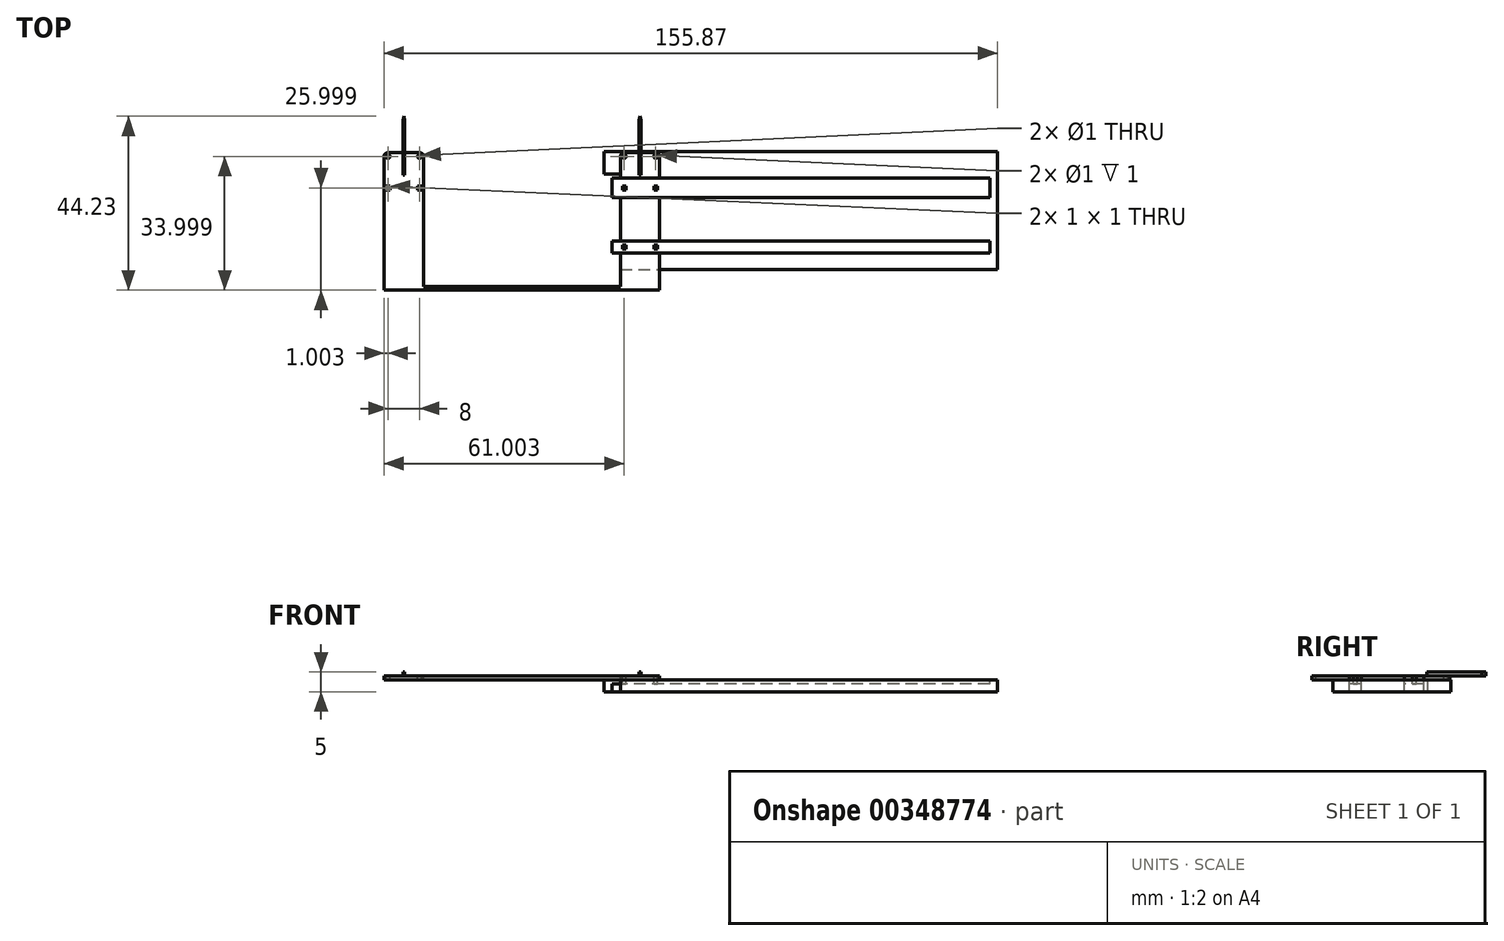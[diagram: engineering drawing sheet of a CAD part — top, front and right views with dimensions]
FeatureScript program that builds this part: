
annotation { "Feature Type Name" : "Feature", "Feature Type Description" : "" }
export const myFeature = defineFeature(function(context is Context, id is Id, definition is map)
    precondition{}
    {
        {
            var Q0;
            Q0=qCreatedBy(makeId("Top.planeOp"),FACE);
            var sketch = newSketch(context, id + "F0", { "sketchPlane" : qUnion([Q0])});
            skLineSegment(sketch, "E0.bottom", {"start": v(4.13, -30.56) * mm, "end": v(14.13, -30.56) * mm});
            skLineSegment(sketch, "E0.top", {"start": v(5.13, -20.56) * mm, "end": v(13.13, -20.56) * mm});
            skLineSegment(sketch, "E0.left", {"start": v(4.13, -30.56) * mm, "end": v(4.13, -21.56) * mm});
            skLineSegment(sketch, "E0.right", {"start": v(14.13, -30.56) * mm, "end": v(14.13, -21.56) * mm});
            skCircle(sketch, "E1", {"center": v(5.13, -21.56) * mm, "radius": 0.5 * mm});
            skLineSegment(sketch, "E2", {"start": v(14.13, -20.56) * mm, "end": v(16.75, -17.94) * mm, "construction": true});
            skCircle(sketch, "E3.MirrorC", {"center": v(13.13, -29.56) * mm, "radius": 0.5 * mm, "construction": true});
            skCircle(sketch, "E4", {"center": v(5.13, -29.56) * mm, "radius": 0.5 * mm, "construction": true});
            skCircle(sketch, "E5", {"center": v(13.13, -21.56) * mm, "radius": 0.5 * mm});
            skPoint(sketch, "E6.visualSharp", {"position": v(4.13, -20.56) * mm});
            skArc(sketch, "E6.filletArc", {"start": v(5.13, -20.56) * mm, "mid": v(4.43, -20.85) * mm, "end": v(4.13, -21.56) * mm});
            skPoint(sketch, "E7.visualSharp", {"position": v(14.13, -20.56) * mm});
            skArc(sketch, "E7.filletArc", {"start": v(14.13, -21.56) * mm, "mid": v(13.84, -20.85) * mm, "end": v(13.13, -20.56) * mm});
            skCircle(sketch, "E8", {"center": v(5.13, -44.56) * mm, "radius": 0.5 * mm, "construction": true});
            skCircle(sketch, "E9", {"center": v(13.13, -44.56) * mm, "radius": 0.5 * mm, "construction": true});
            skLineSegment(sketch, "E10.bottom", {"start": v(5.63, -29.06) * mm, "end": v(4.63, -29.06) * mm});
            skLineSegment(sketch, "E10.top", {"start": v(5.63, -30.06) * mm, "end": v(4.63, -30.06) * mm});
            skLineSegment(sketch, "E10.left", {"start": v(5.63, -29.06) * mm, "end": v(5.63, -30.06) * mm});
            skLineSegment(sketch, "E10.right", {"start": v(4.63, -29.06) * mm, "end": v(4.63, -30.06) * mm});
            skLineSegment(sketch, "E11.bottom", {"start": v(13.63, -29.06) * mm, "end": v(12.63, -29.06) * mm});
            skLineSegment(sketch, "E11.top", {"start": v(13.63, -30.06) * mm, "end": v(12.63, -30.06) * mm});
            skLineSegment(sketch, "E11.left", {"start": v(13.63, -29.06) * mm, "end": v(13.63, -30.06) * mm});
            skLineSegment(sketch, "E11.right", {"start": v(12.63, -29.06) * mm, "end": v(12.63, -30.06) * mm});
            skLineSegment(sketch, "E12.bottom", {"start": v(5.63, -44.06) * mm, "end": v(4.63, -44.06) * mm});
            skLineSegment(sketch, "E12.top", {"start": v(5.63, -45.06) * mm, "end": v(4.63, -45.06) * mm});
            skLineSegment(sketch, "E12.left", {"start": v(5.63, -44.06) * mm, "end": v(5.63, -45.06) * mm});
            skLineSegment(sketch, "E12.right", {"start": v(4.63, -44.06) * mm, "end": v(4.63, -45.06) * mm});
            skLineSegment(sketch, "E13.bottom", {"start": v(13.63, -44.06) * mm, "end": v(12.63, -44.06) * mm});
            skLineSegment(sketch, "E13.top", {"start": v(13.63, -45.06) * mm, "end": v(12.63, -45.06) * mm});
            skLineSegment(sketch, "E13.left", {"start": v(13.63, -44.06) * mm, "end": v(13.63, -45.06) * mm});
            skLineSegment(sketch, "E13.right", {"start": v(12.63, -44.06) * mm, "end": v(12.63, -45.06) * mm});
            skLineSegment(sketch, "E14", {"start": v(-20.87, -13.48) * mm, "end": v(-20.87, -4.13) * mm, "construction": true});
            skLineSegment(sketch, "E15.MirrorCS", {"start": v(-47.37, -45.06) * mm, "end": v(-46.37, -45.06) * mm});
            skLineSegment(sketch, "E16.MirrorCS", {"start": v(-47.37, -44.06) * mm, "end": v(-46.37, -44.06) * mm});
            skLineSegment(sketch, "E17.MirrorCS", {"start": v(-46.37, -29.06) * mm, "end": v(-46.37, -30.06) * mm});
            skLineSegment(sketch, "E18.MirrorCS", {"start": v(-47.37, -30.06) * mm, "end": v(-46.37, -30.06) * mm});
            skLineSegment(sketch, "E19.MirrorCS", {"start": v(-55.37, -30.06) * mm, "end": v(-54.37, -30.06) * mm});
            skLineSegment(sketch, "E20.MirrorCS", {"start": v(-46.37, -44.06) * mm, "end": v(-46.37, -45.06) * mm});
            skLineSegment(sketch, "E21.MirrorCS", {"start": v(-47.37, -29.06) * mm, "end": v(-46.37, -29.06) * mm});
            skLineSegment(sketch, "E22.MirrorCS", {"start": v(-47.37, -44.06) * mm, "end": v(-47.37, -45.06) * mm});
            skCircle(sketch, "E23.MirrorC", {"center": v(-46.87, -29.56) * mm, "radius": 0.5 * mm, "construction": true});
            skLineSegment(sketch, "E24.MirrorCS", {"start": v(-55.37, -29.06) * mm, "end": v(-54.37, -29.06) * mm});
            skCircle(sketch, "E25.MirrorC", {"center": v(-46.87, -44.56) * mm, "radius": 0.5 * mm, "construction": true});
            skLineSegment(sketch, "E26.MirrorCS", {"start": v(-47.37, -29.06) * mm, "end": v(-47.37, -30.06) * mm});
            skLineSegment(sketch, "E27.MirrorCS", {"start": v(-54.37, -44.06) * mm, "end": v(-54.37, -45.06) * mm});
            skLineSegment(sketch, "E28.MirrorCS", {"start": v(-55.37, -44.06) * mm, "end": v(-54.37, -44.06) * mm});
            skCircle(sketch, "E29.MirrorC", {"center": v(-54.87, -29.56) * mm, "radius": 0.5 * mm, "construction": true});
            skLineSegment(sketch, "E30.MirrorCS", {"start": v(-54.37, -29.06) * mm, "end": v(-54.37, -30.06) * mm});
            skLineSegment(sketch, "E31.MirrorCS", {"start": v(-55.37, -29.06) * mm, "end": v(-55.37, -30.06) * mm});
            skLineSegment(sketch, "E32.MirrorCS", {"start": v(-55.37, -44.06) * mm, "end": v(-55.37, -45.06) * mm});
            skCircle(sketch, "E33.MirrorC", {"center": v(-54.87, -44.56) * mm, "radius": 0.5 * mm, "construction": true});
            skCircle(sketch, "E34.MirrorC", {"center": v(-54.87, -21.56) * mm, "radius": 0.5 * mm});
            skLineSegment(sketch, "E35.MirrorCS", {"start": v(-55.37, -45.06) * mm, "end": v(-54.37, -45.06) * mm});
            skArc(sketch, "E36.MirrorCS", {"start": v(-46.87, -20.56) * mm, "mid": v(-46.16, -20.85) * mm, "end": v(-45.87, -21.56) * mm});
            skArc(sketch, "E37.MirrorCS", {"start": v(-55.87, -21.56) * mm, "mid": v(-55.57, -20.85) * mm, "end": v(-54.87, -20.56) * mm});
            skCircle(sketch, "E38.MirrorC", {"center": v(-46.87, -21.56) * mm, "radius": 0.5 * mm});
            skLineSegment(sketch, "E39.MirrorCS", {"start": v(-55.87, -20.56) * mm, "end": v(-58.48, -17.94) * mm, "construction": true});
            skLineSegment(sketch, "E40.MirrorCS", {"start": v(-46.87, -20.56) * mm, "end": v(-54.87, -20.56) * mm});
            skLineSegment(sketch, "E41.MirrorCS", {"start": v(-45.87, -30.56) * mm, "end": v(-55.87, -30.56) * mm});
            skLineSegment(sketch, "E42.MirrorCS", {"start": v(-45.87, -30.56) * mm, "end": v(-45.87, -21.56) * mm});
            skLineSegment(sketch, "E43.MirrorCS", {"start": v(-55.87, -30.56) * mm, "end": v(-55.87, -21.56) * mm});
            skPoint(sketch, "E44.MirrorP", {"position": v(-55.87, -20.56) * mm});
            skPoint(sketch, "E45.MirrorP", {"position": v(-45.87, -20.56) * mm});
            skLineSegment(sketch, "E46.bottom", {"start": v(-45.87, -30.56) * mm, "end": v(4.13, -30.56) * mm});
            skLineSegment(sketch, "E46.top", {"start": v(-45.87, -26.06) * mm, "end": v(4.13, -26.06) * mm});
            skLineSegment(sketch, "E46.left", {"start": v(-45.87, -30.56) * mm, "end": v(-45.87, -26.06) * mm});
            skLineSegment(sketch, "E46.right", {"start": v(4.13, -30.56) * mm, "end": v(4.13, -26.06) * mm});
            skSolve(sketch);
        }
        {
            var Q0;
            Q0=makeQuery(id+"F0.imprint","IMPRINT",FACE,{"disambiguationData":[TD([[makeQuery(id+"F0.imprint","IMPRINT",EDGE,{"derivedFrom":sQuery(id+"F0.wireOp",EDGE,"E0.bottom")}),1.0]])]});
            var Q1;
            Q1=makeQuery(id+"F0.imprint","IMPRINT",FACE,{"disambiguationData":[TD([[makeQuery(id+"F0.imprint","IMPRINT",EDGE,{"derivedFrom":sQuery(id+"F0.wireOp",EDGE,"E17.MirrorCS")}),1.0]])]});
            var Q2;
            Q2=makeQuery(id+"F0.imprint","IMPRINT",FACE,{"disambiguationData":[TD([[makeQuery(id+"F0.imprint","IMPRINT",EDGE,{"derivedFrom":sQuery(id+"F0.wireOp",EDGE,"E46.bottom")}),1.0]])]});
            extrude(context, id + "F1", {"entities" : qUnion([Q0, Q1, Q2]), "oppositeDirection" : true, "depth" : 1 * mm});
        }
        {
            var Q0;
            Q0=makeQuery(id+"F1.opExtrude","CAP_FACE",FACE,{"disambiguationData":[OSD([sQuery(id+"F0.wireOp",EDGE,"E0.bottom"),sQuery(id+"F0.wireOp",EDGE,"E0.top"),sQuery(id+"F0.wireOp",EDGE,"E0.left"),sQuery(id+"F0.wireOp",EDGE,"E0.right"),sQuery(id+"F0.wireOp",EDGE,"E1"),sQuery(id+"F0.wireOp",EDGE,"E3.MirrorC"),sQuery(id+"F0.wireOp",EDGE,"E4"),sQuery(id+"F0.wireOp",EDGE,"E5"),sQuery(id+"F0.wireOp",EDGE,"E6.filletArc"),sQuery(id+"F0.wireOp",EDGE,"E7.filletArc")])],"isStart":true});
            var sketch = newSketch(context, id + "F2", { "sketchPlane" : qUnion([Q0])});
            skLineSegment(sketch, "E47", {"start": v(9.13, -11.33) * mm, "end": v(9.13, -5.3) * mm, "construction": true});
            skPoint(sketch, "E47.startSnap0", {"position": v(9.13, -20.56) * mm});
            skLineSegment(sketch, "E48", {"start": v(9.13, -11.33) * mm, "end": v(8.9, -12.33) * mm});
            skLineSegment(sketch, "E49.MirrorCS", {"start": v(9.13, -11.33) * mm, "end": v(9.37, -12.33) * mm});
            skLineSegment(sketch, "E50", {"start": v(8.9, -12.33) * mm, "end": v(9.37, -12.33) * mm});
            skLineSegment(sketch, "E51.top", {"start": v(8.9, -26.33) * mm, "end": v(9.37, -26.33) * mm});
            skLineSegment(sketch, "E51.left", {"start": v(8.9, -12.33) * mm, "end": v(8.9, -26.33) * mm});
            skLineSegment(sketch, "E51.right", {"start": v(9.37, -12.33) * mm, "end": v(9.37, -26.33) * mm});
            skLineSegment(sketch, "E52.MirrorCS", {"start": v(-50.63, -12.33) * mm, "end": v(-50.63, -26.33) * mm});
            skLineSegment(sketch, "E53.MirrorCS", {"start": v(-51.1, -12.33) * mm, "end": v(-51.1, -26.33) * mm});
            skLineSegment(sketch, "E54.MirrorCS", {"start": v(-50.87, -11.33) * mm, "end": v(-51.1, -12.33) * mm});
            skLineSegment(sketch, "E55.MirrorCS", {"start": v(-50.87, -11.33) * mm, "end": v(-50.63, -12.33) * mm});
            skLineSegment(sketch, "E56.MirrorCS", {"start": v(-50.63, -12.33) * mm, "end": v(-51.1, -12.33) * mm});
            skLineSegment(sketch, "E57.MirrorCS", {"start": v(-50.87, -11.33) * mm, "end": v(-50.87, -5.3) * mm, "construction": true});
            skLineSegment(sketch, "E58.MirrorCS", {"start": v(-50.63, -26.33) * mm, "end": v(-51.1, -26.33) * mm});
            skSolve(sketch);
        }
        {
            var Q0;
            Q0 = qSketchRegion(id + "F2", true);
            extrude(context, id + "F3", {"entities" : qUnion([Q0]), "depth" : 1 * mm});
        }
        {
            var Q0;
            Q0=qCreatedBy(makeId("Top.planeOp"),FACE);
            var sketch = newSketch(context, id + "F4", { "sketchPlane" : qUnion([Q0])});
            skLineSegment(sketch, "E59.bottom", {"start": v(0, -20.29) * mm, "end": v(100, -20.29) * mm});
            skLineSegment(sketch, "E59.top", {"start": v(0, -50.29) * mm, "end": v(100, -50.29) * mm});
            skLineSegment(sketch, "E59.left", {"start": v(0, -20.29) * mm, "end": v(0, -50.29) * mm});
            skLineSegment(sketch, "E59.right", {"start": v(100, -20.29) * mm, "end": v(100, -50.29) * mm});
            skLineSegment(sketch, "E60.bottom", {"start": v(98, -27.06) * mm, "end": v(2, -27.06) * mm});
            skLineSegment(sketch, "E60.top", {"start": v(98, -32.06) * mm, "end": v(2, -32.06) * mm});
            skLineSegment(sketch, "E60.left", {"start": v(98, -27.06) * mm, "end": v(98, -32.06) * mm});
            skLineSegment(sketch, "E60.right", {"start": v(2, -27.06) * mm, "end": v(2, -32.06) * mm});
            skPoint(sketch, "E60.middle", {"position": v(50, -29.56) * mm});
            skPoint(sketch, "E60.middle.positionSnap0", {"position": v(50, -20.29) * mm});
            skPoint(sketch, "E60.centerSnap0", {"position": v(50, -20.29) * mm});
            skLineSegment(sketch, "E61.bottom", {"start": v(2, -43.06) * mm, "end": v(98, -43.06) * mm});
            skLineSegment(sketch, "E61.top", {"start": v(2, -46.06) * mm, "end": v(98, -46.06) * mm});
            skLineSegment(sketch, "E61.left", {"start": v(2, -43.06) * mm, "end": v(2, -46.06) * mm});
            skLineSegment(sketch, "E61.right", {"start": v(98, -43.06) * mm, "end": v(98, -46.06) * mm});
            skPoint(sketch, "E61.middle", {"position": v(50, -44.56) * mm});
            skPoint(sketch, "E62", {"position": v(2, -44.56) * mm});
            skPoint(sketch, "E63", {"position": v(2, -29.56) * mm});
            skSolve(sketch);
        }
        {
            var Q0;
            Q0=makeQuery(id+"F4.imprint","IMPRINT",FACE,{"disambiguationData":[TD([[makeQuery(id+"F4.imprint","IMPRINT",EDGE,{"derivedFrom":sQuery(id+"F4.wireOp",EDGE,"E59.bottom")}),-1.0]])]});
            var Q1;
            Q1=makeQuery(id+"F4.imprint","IMPRINT",FACE,{"disambiguationData":[TD([[makeQuery(id+"F4.imprint","IMPRINT",EDGE,{"derivedFrom":sQuery(id+"F4.wireOp",EDGE,"E61.bottom")}),-1.0]])]});
            var Q2;
            Q2=makeQuery(id+"F4.imprint","IMPRINT",FACE,{"disambiguationData":[TD([[makeQuery(id+"F4.imprint","IMPRINT",EDGE,{"derivedFrom":sQuery(id+"F4.wireOp",EDGE,"E60.bottom")}),1.0]])]});
            extrude(context, id + "F5", {"entities" : qUnion([Q0, Q1, Q2]), "oppositeDirection" : true, "depth" : 4 * mm, "hasSecondDirection" : true, "secondDirectionOppositeDirection" : true, "secondDirectionDepth" : 1 * mm});
        }
        {
            var Q0;
            Q0=makeQuery(id+"F1.opExtrude","SWEPT_FACE",FACE,{"disambiguationData":[OSD([sQuery(id+"F0.wireOp",EDGE,"E0.bottom")])]});
            extrude(context, id + "F6", {"entities" : qUnion([Q0]), "operationType" : NewBodyOperationType.ADD, "depth" : 25 * mm});
        }
        {
            var Q0;
            Q0=makeQuery(id+"F4.imprint","IMPRINT",FACE,{"disambiguationData":[TD([[makeQuery(id+"F4.imprint","IMPRINT",EDGE,{"derivedFrom":sQuery(id+"F4.wireOp",EDGE,"E60.bottom")}),1.0]])]});
            var Q1;
            Q1=makeQuery(id+"F4.imprint","IMPRINT",FACE,{"disambiguationData":[TD([[makeQuery(id+"F4.imprint","IMPRINT",EDGE,{"derivedFrom":sQuery(id+"F4.wireOp",EDGE,"E61.bottom")}),-1.0]])]});
            extrude(context, id + "F7", {"entities" : qUnion([Q0, Q1]), "operationType" : NewBodyOperationType.REMOVE, "oppositeDirection" : true, "depth" : 2 * mm});
        }
        {
            var Q0;
            Q0=makeQuery(id+"F0.imprint","IMPRINT",FACE,{"disambiguationData":[TD([[makeQuery(id+"F0.imprint","IMPRINT",EDGE,{"derivedFrom":sQuery(id+"F0.wireOp",EDGE,"E13.bottom")}),1.0]])]});
            var Q1;
            Q1=makeQuery(id+"F0.imprint","IMPRINT",FACE,{"disambiguationData":[TD([[makeQuery(id+"F0.imprint","IMPRINT",EDGE,{"derivedFrom":sQuery(id+"F0.wireOp",EDGE,"E12.bottom")}),1.0]])]});
            var Q2;
            Q2=makeQuery(id+"F0.imprint","IMPRINT",FACE,{"disambiguationData":[TD([[makeQuery(id+"F0.imprint","IMPRINT",EDGE,{"derivedFrom":sQuery(id+"F0.wireOp",EDGE,"E10.bottom")}),1.0]])]});
            var Q3;
            Q3=makeQuery(id+"F0.imprint","IMPRINT",FACE,{"disambiguationData":[TD([[makeQuery(id+"F0.imprint","IMPRINT",EDGE,{"derivedFrom":sQuery(id+"F0.wireOp",EDGE,"E11.bottom")}),1.0]])]});
            var Q4;
            Q4=sQuery(id+"F0.wireOp",EDGE,"E8");
            var Q5;
            Q5=sQuery(id+"F0.wireOp",EDGE,"E9");
            var Q6;
            Q6=makeQuery(id+"F7.boolean.opBoolean","COPY",FACE,{"derivedFrom":makeQuery(id+"F7.opExtrude","CAP_FACE",FACE,{"disambiguationData":[OSD([sQuery(id+"F4.wireOp",EDGE,"E60.bottom"),sQuery(id+"F4.wireOp",EDGE,"E60.top"),sQuery(id+"F4.wireOp",EDGE,"E60.left"),sQuery(id+"F4.wireOp",EDGE,"E60.right")])],"isStart":false})});
            extrude(context, id + "F8", {"entities" : qUnion([Q0, Q1, Q2, Q3]), "operationType" : NewBodyOperationType.ADD, "surfaceEntities" : qUnion([Q4, Q5]), "endBound" : BoundingType.UP_TO_SURFACE, "oppositeDirection" : true, "endBoundEntityFace" : qUnion([Q6]), "depth" : 1 * mm});
        }
        {
            var Q0;
            {var subQ0=sQuery(id+"F0.wireOp",EDGE,"E11.right");var subQ1=sQuery(id+"F0.wireOp",EDGE,"E11.left");var subQ2=sQuery(id+"F0.wireOp",EDGE,"E11.top");var subQ3=sQuery(id+"F0.wireOp",EDGE,"E11.bottom");var subQ4=sQuery(id+"F0.wireOp",EDGE,"E10.right");var subQ5=sQuery(id+"F0.wireOp",EDGE,"E10.left");var subQ6=sQuery(id+"F0.wireOp",EDGE,"E10.top");var subQ7=sQuery(id+"F0.wireOp",EDGE,"E10.bottom");var subQ8=sQuery(id+"F0.wireOp",EDGE,"E0.bottom");Q0=makeQuery(id+"F8.boolean.opBoolean","MERGE",FACE,{"derivedFrom":[makeQuery(id+"F6.boolean.opBoolean","MERGE",FACE,{"derivedFrom":[makeQuery(id+"F1.opExtrude","CAP_FACE",FACE,{"disambiguationData":[OSD([subQ8,sQuery(id+"F0.wireOp",EDGE,"E0.top"),sQuery(id+"F0.wireOp",EDGE,"E0.left"),sQuery(id+"F0.wireOp",EDGE,"E0.right"),sQuery(id+"F0.wireOp",EDGE,"E1"),sQuery(id+"F0.wireOp",EDGE,"E5"),sQuery(id+"F0.wireOp",EDGE,"E6.filletArc"),sQuery(id+"F0.wireOp",EDGE,"E7.filletArc"),subQ7,subQ6,subQ5,subQ4,subQ3,subQ2,subQ1,subQ0])],"isStart":true}),makeQuery(id+"F6.opExtrude","SWEPT_FACE",FACE,{"disambiguationData":[OSD([subQ8]),TDD([makeQuery(id+"F1.opExtrude","CAP_EDGE",EDGE,{"disambiguationData":[OSD([subQ8])],"isStart":true})])]})]}),makeQuery(id+"F8.opExtrude","CAP_FACE",FACE,{"disambiguationData":[OSD([subQ7,subQ6,subQ5,subQ4])],"isStart":true}),makeQuery(id+"F8.opExtrude","CAP_FACE",FACE,{"disambiguationData":[OSD([subQ3,subQ2,subQ1,subQ0])],"isStart":true})]});}
            var sketch = newSketch(context, id + "F9", { "sketchPlane" : qUnion([Q0])});
            skLineSegment(sketch, "E64.bottom", {"start": v(-45.87, -26.06) * mm, "end": v(4.13, -26.06) * mm});
            skLineSegment(sketch, "E64.top", {"start": v(-45.87, -54.56) * mm, "end": v(4.13, -54.56) * mm});
            skLineSegment(sketch, "E64.left", {"start": v(-45.87, -26.06) * mm, "end": v(-45.87, -54.56) * mm});
            skLineSegment(sketch, "E64.right", {"start": v(4.13, -26.06) * mm, "end": v(4.13, -54.56) * mm});
            skSolve(sketch);
        }
        {
            var Q0;
            Q0=makeQuery(id+"F9.imprint","IMPRINT",FACE,{"disambiguationData":[TD([[makeQuery(id+"F9.imprint","IMPRINT",EDGE,{"derivedFrom":sQuery(id+"F9.wireOp",EDGE,"E64.bottom")}),-1.0]])]});
            extrude(context, id + "F10", {"entities" : qUnion([Q0]), "operationType" : NewBodyOperationType.REMOVE, "oppositeDirection" : true, "depth" : 25 * mm});
        }
    });
